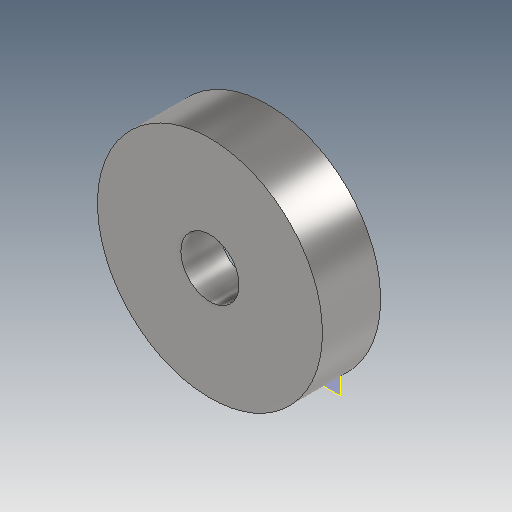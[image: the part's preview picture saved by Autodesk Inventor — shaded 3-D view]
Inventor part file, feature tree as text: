
AUTODESK INVENTOR PART (.ipt)
format: ipt  version: 2020.3 (Build 243373010, 373A)  size: 200,192 bytes
history: native  units: mm
features: sketch x8, extrude x6, plane x1, hole x1, projected_geometry x1
ambient origin geometry x8: Origin, YZ Plane, XZ Plane, XY Plane, X Axis, Y Axis, Z Axis, Center Point
bodies: Solid1 (feature_tree)
feature tree (17):
  extrude  "Extrusion1"  Depth=45.375mm
  extrude  "Extrusion2"  Depth=10.0mm TaperAngle=0.0deg
  plane  "Work Plane1"
  extrude  "Extrusion6"  Depth=10.0mm TaperAngle=0.0deg
  extrude  "Extrusion7"  Depth=10.0mm TaperAngle=0.0deg
  extrude  "Extrusion8"  Depth=2.5mm
  extrude  "Extrusion9"  Depth=10.0mm TaperAngle=0.0deg
  hole  "Hole1"  [1 undecoded]
  sketch  "Sketch10"  dims[d40=58.0mm d41=51.6875mm d42=40.0mm d44=360.0deg d46=2.459mm d47=6.0mm d48=4.0mm d49=2.0mm d50=90.0deg d51=8.8mm d52=0.0mm d53=6.3125mm]
  sketch  "Sketch1"  dims[d0=48.0mm d2=45.375mm]
  sketch  "Sketch2"  dims[d3=5.0mm d4=0.0mm d5=10.0mm d6=0.0mm]
  sketch  "Sketch6"  dims[d29=15.0mm d30=10.0mm d31=0.0mm]
  sketch  "Sketch7"  dims[d32=2.5mm d33=0.0mm d34=38.25mm]
  projected_geometry  "Projected Loop1"
  sketch  "Sketch8"  dims[d35=58.0mm d36=10.0mm d37=0.0mm]
  sketch  "Sketch9"  dims[d38=45.0deg d39=45.375mm]
  sketch  "Sketch3"  dims[d8=40.0mm d9=360.0deg d10=0.35mm d11=0.35mm d27=10.0mm d28=0.0mm]
note: 1 required parameter value undecoded (feature->parameter linkage not recoverable at this tier; creation-order binding heuristic only, values carry confidence <= 0.55)
